# Revit family: VP103UB
name_source: partatom
category: Generic Models
revit_build: Autodesk Revit MEP 2013 (Build: 20130531_2115(x64)
units: mm (PartAtom-declared; Revit-internal decimal feet)

## types (1)
- Zip Varipoint III_ model_VP103UB
    BMS Links = No
    Base Unit Finish = White impact resistant plastic
    Button Interface = No
    Capacity = 10.0L
    Control Thermostat Range = 50°C,  65°C   80°C
    Enclosure Rating = IP24
    External Material = The casing is constructed of impact resistant plastic
    Gross Weight (When Full) = 16.5kg
    Heat Up Time = 11mins
    Insulation Material = Heat losses are minimised by high efficiency CFCfree polyurethane foam insulation
the high efficiency CFC free polyurethane foam insulation.
the high efficiency CFC free polyurethane foam insulation.
    Internal Filter (if fitted) = No
    Mains Pressure Limiting Valve = offered as accessory
    Mains Water Connection = 1/2" BSP
    Mains Water Pressure _ Maximum = 0.55 Mpa
    Manufacturer = Zip Industries(UK) Ltd
    Max. Stored Water Temperature = 80°C
    Model = VP103UB
    Net Weight = 6.5kg
    Overall Height = 452
    Overall Length/Depth/Circumference = 285
    Overall Width = 300
    Power Rating = 2.2 kW
    Power Supply (Voltage) = 230 (V~)
    Product Range = Wall Mounted
    Programmable Function Parameters = No
    Programmable Safety Features = No
    Shape = Rectangular
    Standby Power Loss (idle mode) = Not Known
    Supply Phase = 1
    Tank Construction Material = The Tank is constructed from heavy guage copper tested to 1.6MPa (16 bar),
maximum working pressure 0.55 MPa (5.5 bar
    Type = Direct unvented water heater
    Type Comments = Direct unvented water heater
    URL = www.zipindustries.co.uk
    Unit Access Clearance Bottom = 400mm
    Unit Access Clearance Top = 250mm
    WRAS Approved = Yes
    Warranty ID = Zip Heaters (UK) Ltd warrants that, should any part fail within 12 calendar months of installation
    Wireless (WIFI) = No

## geometry (parser evidence)
native form markers: Sweep x1
no freeform markers — native parametric forms only
